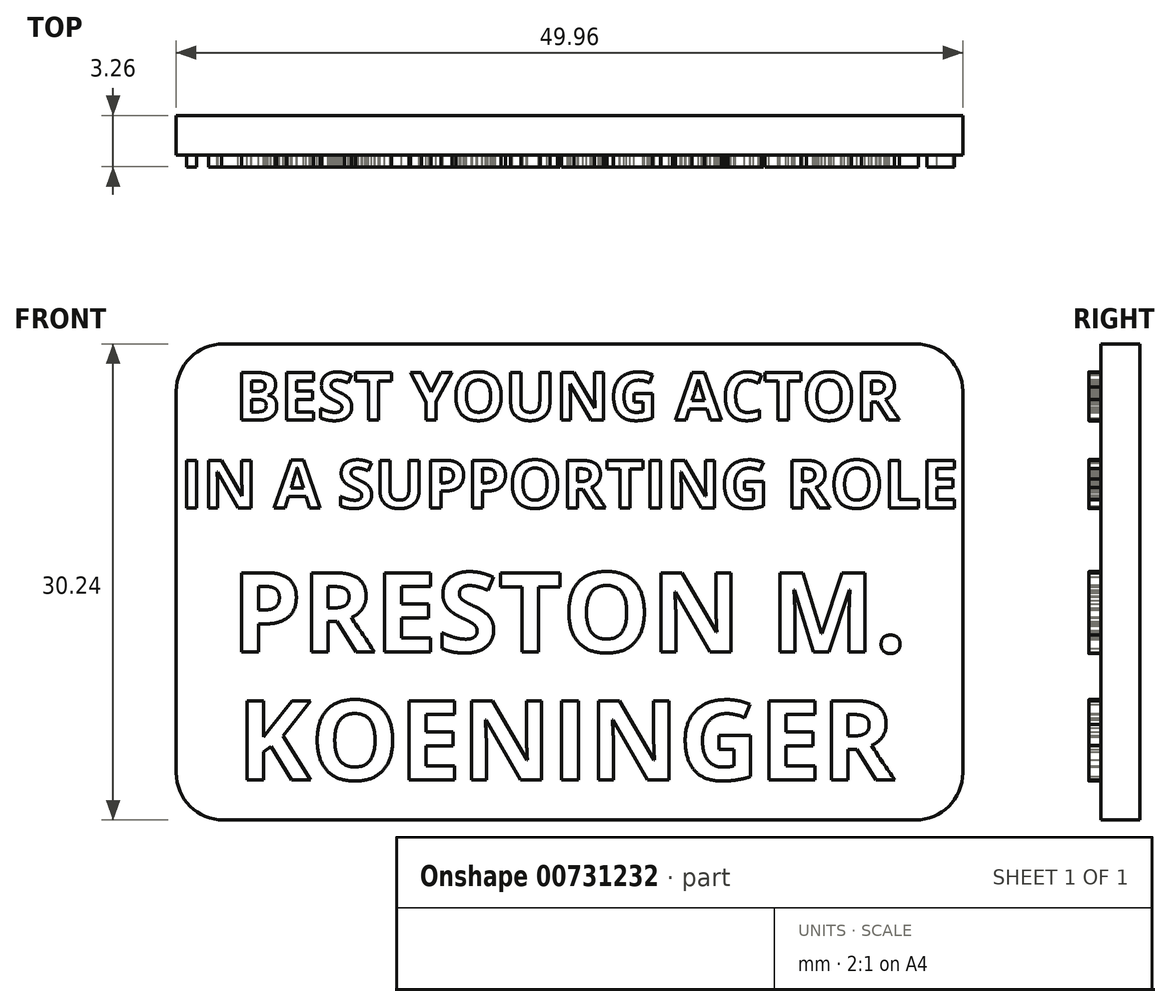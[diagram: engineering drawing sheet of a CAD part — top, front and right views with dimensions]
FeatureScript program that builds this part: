
annotation { "Feature Type Name" : "Feature", "Feature Type Description" : "" }
export const myFeature = defineFeature(function(context is Context, id is Id, definition is map)
    precondition{}
    {
        {
            var Q0;
            Q0=qCreatedBy(makeId("Top.planeOp"),FACE);
            var sketch = newSketch(context, id + "F0", { "sketchPlane" : qUnion([Q0])});
            skLineSegment(sketch, "E0.bottom", {"start": v(27, 13.5) * mm, "end": v(-27, 13.5) * mm});
            skLineSegment(sketch, "E0.top", {"start": v(27, -13.5) * mm, "end": v(-27, -13.5) * mm});
            skLineSegment(sketch, "E0.left", {"start": v(27, 13.5) * mm, "end": v(27, -13.5) * mm});
            skLineSegment(sketch, "E0.right", {"start": v(-27, 13.5) * mm, "end": v(-27, -13.5) * mm});
            skPoint(sketch, "E0.middle", {"position": v(0, 0) * mm});
            skLineSegment(sketch, "E1.bottom", {"start": v(37, 23.5) * mm, "end": v(-37, 23.5) * mm});
            skLineSegment(sketch, "E1.top", {"start": v(37, -23.5) * mm, "end": v(-37, -23.5) * mm});
            skLineSegment(sketch, "E1.left", {"start": v(37, 23.5) * mm, "end": v(37, -23.5) * mm});
            skLineSegment(sketch, "E1.right", {"start": v(-37, 23.5) * mm, "end": v(-37, -23.5) * mm});
            skLineSegment(sketch, "E2.bottom", {"start": v(6, 3) * mm, "end": v(-6, 3) * mm, "construction": true});
            skLineSegment(sketch, "E2.top", {"start": v(6, -3) * mm, "end": v(-6, -3) * mm, "construction": true});
            skLineSegment(sketch, "E2.left", {"start": v(6, 3) * mm, "end": v(6, -3) * mm, "construction": true});
            skLineSegment(sketch, "E2.right", {"start": v(-6, 3) * mm, "end": v(-6, -3) * mm, "construction": true});
            skLineSegment(sketch, "E3.0", {"start": v(6.25, 3.25) * mm, "end": v(-6.25, 3.25) * mm});
            skLineSegment(sketch, "E3.1", {"start": v(6.25, 3.25) * mm, "end": v(6.25, -3.25) * mm});
            skLineSegment(sketch, "E3.2", {"start": v(6.25, -3.25) * mm, "end": v(-6.25, -3.25) * mm});
            skLineSegment(sketch, "E3.3", {"start": v(-6.25, 3.25) * mm, "end": v(-6.25, -3.25) * mm});
            skSolve(sketch);
        }
        {
            var Q0;
            Q0=makeQuery(id+"F0.imprint","IMPRINT",FACE,{"disambiguationData":[TD([[makeQuery(id+"F0.imprint","IMPRINT",EDGE,{"derivedFrom":sQuery(id+"F0.wireOp",EDGE,"E0.bottom")}),-1.0]])]});
            var Q1;
            Q1=makeQuery(id+"F0.imprint","IMPRINT",FACE,{"disambiguationData":[TD([[makeQuery(id+"F0.imprint","IMPRINT",EDGE,{"derivedFrom":sQuery(id+"F0.wireOp",EDGE,"E0.bottom")}),1.0]])]});
            var Q2;
            Q2=makeQuery(id+"F0.imprint","IMPRINT",FACE,{"disambiguationData":[TD([[makeQuery(id+"F0.imprint","IMPRINT",EDGE,{"derivedFrom":sQuery(id+"F0.wireOp",EDGE,"E3.0")}),1.0]])]});
            extrude(context, id + "F1", {"entities" : qUnion([Q0, Q1, Q2]), "depth" : 12 * mm, "offsetDistance" : 25.4 * mm});
        }
        {
            var Q0;
            Q0=makeQuery(id+"F1.opExtrude","CAP_FACE",FACE,{"disambiguationData":[OSD([sQuery(id+"F0.wireOp",EDGE,"E1.bottom"),sQuery(id+"F0.wireOp",EDGE,"E1.top"),sQuery(id+"F0.wireOp",EDGE,"E1.left"),sQuery(id+"F0.wireOp",EDGE,"E1.right")])],"isStart":false});
            var sketch = newSketch(context, id + "F2", { "sketchPlane" : qUnion([Q0])});
            skLineSegment(sketch, "E4.0", {"start": v(27, 13.5) * mm, "end": v(-27, 13.5) * mm});
            skLineSegment(sketch, "E5.0", {"start": v(-27, 13.5) * mm, "end": v(-27, -13.5) * mm});
            skLineSegment(sketch, "E6.0", {"start": v(27, -13.5) * mm, "end": v(-27, -13.5) * mm});
            skLineSegment(sketch, "E7.0", {"start": v(27, 13.5) * mm, "end": v(27, -13.5) * mm});
            skSolve(sketch);
        }
        {
            var Q0;
            Q0 = qSketchRegion(id + "F2", true);
            extrude(context, id + "F3", {"entities" : qUnion([Q0]), "operationType" : NewBodyOperationType.ADD, "depth" : 32 * mm, "offsetDistance" : 25.4 * mm});
        }
        {
            var Q0;
            Q0=makeQuery(id+"F3.opExtrude","CAP_FACE",FACE,{"disambiguationData":[OSD([sQuery(id+"F2.wireOp",EDGE,"E4.0"),sQuery(id+"F2.wireOp",EDGE,"E5.0"),sQuery(id+"F2.wireOp",EDGE,"E6.0"),sQuery(id+"F2.wireOp",EDGE,"E7.0")])],"isStart":false});
            var sketch = newSketch(context, id + "F4", { "sketchPlane" : qUnion([Q0])});
            skLineSegment(sketch, "E8.0", {"start": v(6.25, 3.25) * mm, "end": v(-6.25, 3.25) * mm});
            skLineSegment(sketch, "E9.0", {"start": v(-6.25, 3.25) * mm, "end": v(-6.25, -3.25) * mm});
            skLineSegment(sketch, "E10.0", {"start": v(6.25, -3.25) * mm, "end": v(-6.25, -3.25) * mm});
            skLineSegment(sketch, "E11.0", {"start": v(6.25, 3.25) * mm, "end": v(6.25, -3.25) * mm});
            skSolve(sketch);
        }
        {
            var Q0;
            Q0 = qSketchRegion(id + "F4", true);
            extrude(context, id + "F5", {"entities" : qUnion([Q0]), "operationType" : NewBodyOperationType.REMOVE, "oppositeDirection" : true, "depth" : 1 * mm, "offsetDistance" : 25.4 * mm});
        }
        {
            var Q0;
            Q0=makeQuery(id+"F3.opExtrude","SWEPT_FACE",FACE,{"disambiguationData":[OSD([sQuery(id+"F2.wireOp",EDGE,"E6.0")])]});
            var sketch = newSketch(context, id + "F6", { "sketchPlane" : qUnion([Q0])});
            skText(sketch, "E12", { "text": "BEST YOUNG ACTOR", "fontName": "OpenSans-Bold.ttf"});
            skText(sketch, "E13", { "text": "IN A SUPPORTING ROLE", "fontName": "OpenSans-Bold.ttf"});
            skLineSegment(sketch, "E14", {"start": v(0, 44) * mm, "end": v(0, 40.95) * mm, "construction": true});
            skLineSegment(sketch, "E15", {"start": v(0, 37.9) * mm, "end": v(0, 35.36) * mm, "construction": true});
            skText(sketch, "E16", { "text": "PRESTON M.", "fontName": "OpenSans-Bold.ttf"});
            skLineSegment(sketch, "E17", {"start": v(0, 32.32) * mm, "end": v(0, 28.25) * mm, "construction": true});
            skText(sketch, "E18", { "text": "KOENINGER", "fontName": "OpenSans-Bold.ttf"});
            skLineSegment(sketch, "E19", {"start": v(0, 23.17) * mm, "end": v(0, 20.12) * mm, "construction": true});
            const initialGuessF6  = {"E12": [-0.02121, 0.0379, 1, 0, 0.00305], "E13": [-0.0247, 0.03232, 1, 0, 0.00305], "E16": [-0.02146, 0.02317, 1, 0, 0.00508], "E18": [-0.02112, 0.01504, 1, 0, 0.00508]};
            skSetInitialGuess(sketch, initialGuessF6);
            skSolve(sketch);
        }
        {
            var Q0;
            Q0=makeQuery(id+"F1.opExtrude","SWEPT_EDGE",EDGE,{"disambiguationData":[OSD([sQuery(id+"F0.wireOp",EDGE,"E1.top"),sQuery(id+"F0.wireOp",EDGE,"E1.right")])]});
            var Q1;
            Q1=makeQuery(id+"F1.opExtrude","SWEPT_EDGE",EDGE,{"disambiguationData":[OSD([sQuery(id+"F0.wireOp",EDGE,"E1.top"),sQuery(id+"F0.wireOp",EDGE,"E1.left")])]});
            var Q2;
            Q2=makeQuery(id+"F1.opExtrude","SWEPT_EDGE",EDGE,{"disambiguationData":[OSD([sQuery(id+"F0.wireOp",EDGE,"E1.bottom"),sQuery(id+"F0.wireOp",EDGE,"E1.left")])]});
            var Q3;
            Q3=makeQuery(id+"F1.opExtrude","SWEPT_EDGE",EDGE,{"disambiguationData":[OSD([sQuery(id+"F0.wireOp",EDGE,"E1.bottom"),sQuery(id+"F0.wireOp",EDGE,"E1.right")])]});
            fillet(context, id + "F7", {"entities" : qUnion([Q0, Q1, Q2, Q3]), "radius" : 3.56 * mm, "tangentPropagation" : true, "allowEdgeOverflow" : false});
        }
        {
            var Q0;
            Q0=makeQuery(id+"F3.opExtrude","SWEPT_EDGE",EDGE,{"disambiguationData":[OSD([sQuery(id+"F2.wireOp",EDGE,"E5.0"),sQuery(id+"F2.wireOp",EDGE,"E6.0")])]});
            var Q1;
            Q1=makeQuery(id+"F3.opExtrude","SWEPT_EDGE",EDGE,{"disambiguationData":[OSD([sQuery(id+"F2.wireOp",EDGE,"E6.0"),sQuery(id+"F2.wireOp",EDGE,"E7.0")])]});
            var Q2;
            Q2=makeQuery(id+"F3.opExtrude","SWEPT_EDGE",EDGE,{"disambiguationData":[OSD([sQuery(id+"F2.wireOp",EDGE,"E4.0"),sQuery(id+"F2.wireOp",EDGE,"E7.0")])]});
            var Q3;
            Q3=makeQuery(id+"F3.opExtrude","SWEPT_EDGE",EDGE,{"disambiguationData":[OSD([sQuery(id+"F2.wireOp",EDGE,"E4.0"),sQuery(id+"F2.wireOp",EDGE,"E5.0")])]});
            fillet(context, id + "F8", {"entities" : qUnion([Q0, Q1, Q2, Q3]), "radius" : 1.52 * mm, "tangentPropagation" : true, "allowEdgeOverflow" : false});
        }
        {
            var Q0;
            Q0=makeQuery(id+"F3.opExtrude","CAP_EDGE",EDGE,{"disambiguationData":[OSD([sQuery(id+"F2.wireOp",EDGE,"E6.0")])],"isStart":false});
            var Q1;
            Q1=makeQuery(id+"F1.opExtrude","CAP_EDGE",EDGE,{"disambiguationData":[OSD([sQuery(id+"F0.wireOp",EDGE,"E1.top")])],"isStart":false});
            fillet(context, id + "F9", {"entities" : qUnion([Q0, Q1]), "radius" : 0.76 * mm, "tangentPropagation" : true, "allowEdgeOverflow" : false});
        }
        {
            var Q0;
            Q0=makeQuery(id+"F1.opExtrude","CAP_FACE",FACE,{"disambiguationData":[OSD([sQuery(id+"F0.wireOp",EDGE,"E1.bottom"),sQuery(id+"F0.wireOp",EDGE,"E1.top"),sQuery(id+"F0.wireOp",EDGE,"E1.left"),sQuery(id+"F0.wireOp",EDGE,"E1.right")])],"isStart":true});
            shell(context, id + "F10", {"entities" : qUnion([Q0]), "thickness" : 2.5 * mm});
        }
        {
            var Q0;
            Q0 = qSketchRegion(id + "F6", true);
            extrude(context, id + "F11", {"entities" : qUnion([Q0]), "operationType" : NewBodyOperationType.ADD, "depth" : 0.76 * mm, "offsetDistance" : 25.4 * mm});
        }
        {
            var Q0;
            Q0=qCreatedBy(makeId("Front.planeOp"),FACE);
            var sketch = newSketch(context, id + "F12", { "sketchPlane" : qUnion([Q0])});
            skLineSegment(sketch, "E20.bottom", {"start": v(-21.98, 42.74) * mm, "end": v(21.98, 42.74) * mm});
            skLineSegment(sketch, "E20.top", {"start": v(-21.98, 12.5) * mm, "end": v(21.98, 12.5) * mm});
            skLineSegment(sketch, "E20.left", {"start": v(-24.98, 39.74) * mm, "end": v(-24.98, 15.5) * mm});
            skLineSegment(sketch, "E20.right", {"start": v(24.98, 39.74) * mm, "end": v(24.98, 15.5) * mm});
            skPoint(sketch, "E21.visualSharp", {"position": v(-24.98, 42.74) * mm});
            skArc(sketch, "E21.filletArc", {"start": v(-21.98, 42.74) * mm, "mid": v(-24.1, 41.86) * mm, "end": v(-24.98, 39.74) * mm});
            skPoint(sketch, "E22.visualSharp", {"position": v(-24.98, 12.5) * mm});
            skArc(sketch, "E22.filletArc", {"start": v(-24.98, 15.5) * mm, "mid": v(-24.1, 13.38) * mm, "end": v(-21.98, 12.5) * mm});
            skPoint(sketch, "E23.visualSharp", {"position": v(24.98, 12.5) * mm});
            skArc(sketch, "E23.filletArc", {"start": v(21.98, 12.5) * mm, "mid": v(24.1, 13.38) * mm, "end": v(24.98, 15.5) * mm});
            skPoint(sketch, "E24.visualSharp", {"position": v(24.98, 42.74) * mm});
            skArc(sketch, "E24.filletArc", {"start": v(24.98, 39.74) * mm, "mid": v(24.1, 41.86) * mm, "end": v(21.98, 42.74) * mm});
            skLineSegment(sketch, "E25.bottom", {"start": v(-40.66, -3) * mm, "end": v(41.23, -3) * mm});
            skLineSegment(sketch, "E25.top", {"start": v(-40.66, 46.38) * mm, "end": v(41.23, 46.38) * mm});
            skLineSegment(sketch, "E25.left", {"start": v(-40.66, -3) * mm, "end": v(-40.66, 46.38) * mm});
            skLineSegment(sketch, "E25.right", {"start": v(41.23, -3) * mm, "end": v(41.23, 46.38) * mm});
            skSolve(sketch);
        }
        {
            var Q0;
            Q0 = qSketchRegion(id + "F12", true);
            extrude(context, id + "F13", {"entities" : qUnion([Q0]), "operationType" : NewBodyOperationType.REMOVE, "endBound" : BoundingType.THROUGH_ALL, "oppositeDirection" : true, "depth" : 25.4 * mm, "offsetDistance" : 25.4 * mm, "hasSecondDirection" : true, "secondDirectionBound" : SecondDirectionBoundingType.THROUGH_ALL, "secondDirectionOppositeDirection" : false, "secondDirectionDepth" : 25.4 * mm});
        }
        {
            var Q0;
            Q0=makeQuery(id+"F13.boolean.opBoolean","COPY",FACE,{"derivedFrom":makeQuery(id+"F13.opExtrude","SWEPT_FACE",FACE,{"disambiguationData":[OSD([sQuery(id+"F12.wireOp",EDGE,"E20.bottom")])]})});
            var sketch = newSketch(context, id + "F14", { "sketchPlane" : qUnion([Q0])});
            skPoint(sketch, "E26.0", {"position": v(-24.4, -11) * mm});
            skLineSegment(sketch, "E27.bottom", {"start": v(-34.03, -11) * mm, "end": v(29.71, -11) * mm});
            skLineSegment(sketch, "E27.top", {"start": v(-34.03, 18.37) * mm, "end": v(29.71, 18.37) * mm});
            skLineSegment(sketch, "E27.left", {"start": v(-34.03, -11) * mm, "end": v(-34.03, 18.37) * mm});
            skLineSegment(sketch, "E27.right", {"start": v(29.71, -11) * mm, "end": v(29.71, 18.37) * mm});
            skSolve(sketch);
        }
        {
            var Q0;
            Q0 = qSketchRegion(id + "F14", true);
            extrude(context, id + "F15", {"entities" : qUnion([Q0]), "operationType" : NewBodyOperationType.REMOVE, "endBound" : BoundingType.THROUGH_ALL, "oppositeDirection" : true, "depth" : 25.4 * mm, "offsetDistance" : 25.4 * mm});
        }
    });
